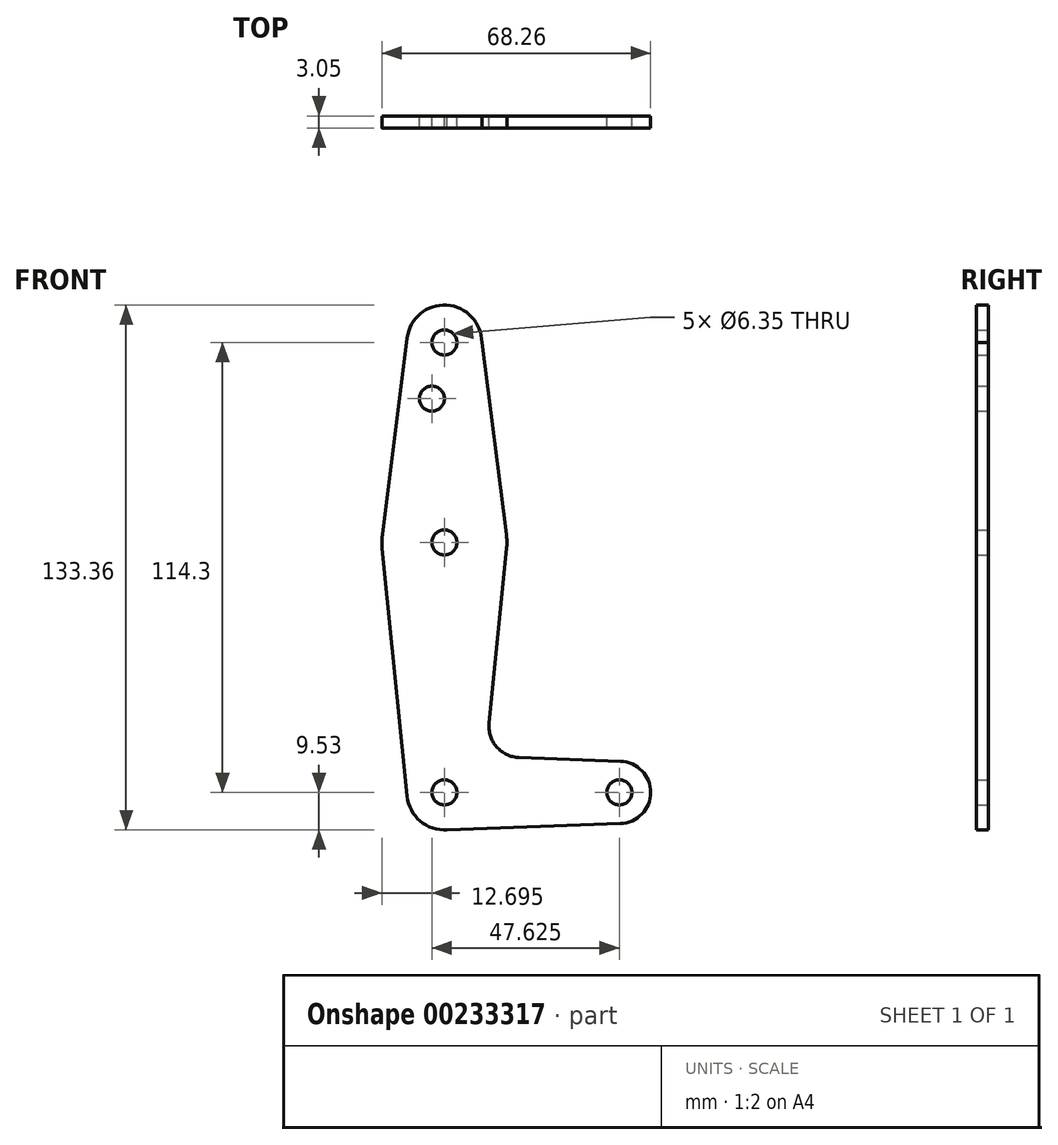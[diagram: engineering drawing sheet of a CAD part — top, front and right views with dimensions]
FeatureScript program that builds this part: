
annotation { "Feature Type Name" : "Feature", "Feature Type Description" : "" }
export const myFeature = defineFeature(function(context is Context, id is Id, definition is map)
    precondition{}
    {
        {
            var Q0;
            Q0=qCreatedBy(makeId("Front.planeOp"),FACE);
            var sketch = newSketch(context, id + "F0", { "sketchPlane" : qUnion([Q0])});
            skLineSegment(sketch, "E0", {"start": v(0, 114.3) * mm, "end": v(0, 0) * mm, "construction": true});
            skCircle(sketch, "E1", {"center": v(0, 114.3) * mm, "radius": 9.53 * mm});
            skCircle(sketch, "E2", {"center": v(0, 63.5) * mm, "radius": 15.88 * mm});
            skCircle(sketch, "E3", {"center": v(0, 0) * mm, "radius": 9.53 * mm});
            skLineSegment(sketch, "E4", {"start": v(0, 0) * mm, "end": v(44.45, 0) * mm, "construction": true});
            skCircle(sketch, "E5", {"center": v(44.45, 0) * mm, "radius": 7.94 * mm});
            skLineSegment(sketch, "E6", {"start": v(9.53, 114.3) * mm, "end": v(15.75, 65.5) * mm});
            skPoint(sketch, "E7.startSnap0", {"position": v(0, 57.15) * mm});
            skLineSegment(sketch, "E8", {"start": v(-15.8, 61.91) * mm, "end": v(-9.48, -0.95) * mm});
            skLineSegment(sketch, "E9", {"start": v(15.8, 61.91) * mm, "end": v(11.34, 17.6) * mm});
            skLineSegment(sketch, "E10", {"start": v(-9.45, 115.5) * mm, "end": v(-15.75, 65.48) * mm});
            skLineSegment(sketch, "E11", {"start": v(0, -9.53) * mm, "end": v(44.73, -7.93) * mm});
            skCircle(sketch, "E12", {"center": v(0, 0) * mm, "radius": 3.18 * mm});
            skCircle(sketch, "E13", {"center": v(44.45, 0) * mm, "radius": 3.18 * mm});
            skCircle(sketch, "E14", {"center": v(0, 63.5) * mm, "radius": 3.18 * mm});
            skCircle(sketch, "E15", {"center": v(0, 114.3) * mm, "radius": 3.18 * mm});
            skCircle(sketch, "E16", {"center": v(-3.17, 100.03) * mm, "radius": 3.18 * mm});
            skLineSegment(sketch, "E17", {"start": v(18.97, 8.85) * mm, "end": v(44.73, 7.93) * mm});
            skArc(sketch, "E18.filletArc", {"start": v(11.34, 17.6) * mm, "mid": v(13.26, 11.57) * mm, "end": v(18.97, 8.85) * mm});
            skSolve(sketch);
        }
        {
            var Q0;
            Q0 = qSketchRegion(id + "F0", true);
            extrude(context, id + "F1", {"entities" : qUnion([Q0]), "depth" : 3.05 * mm});
        }
    });
